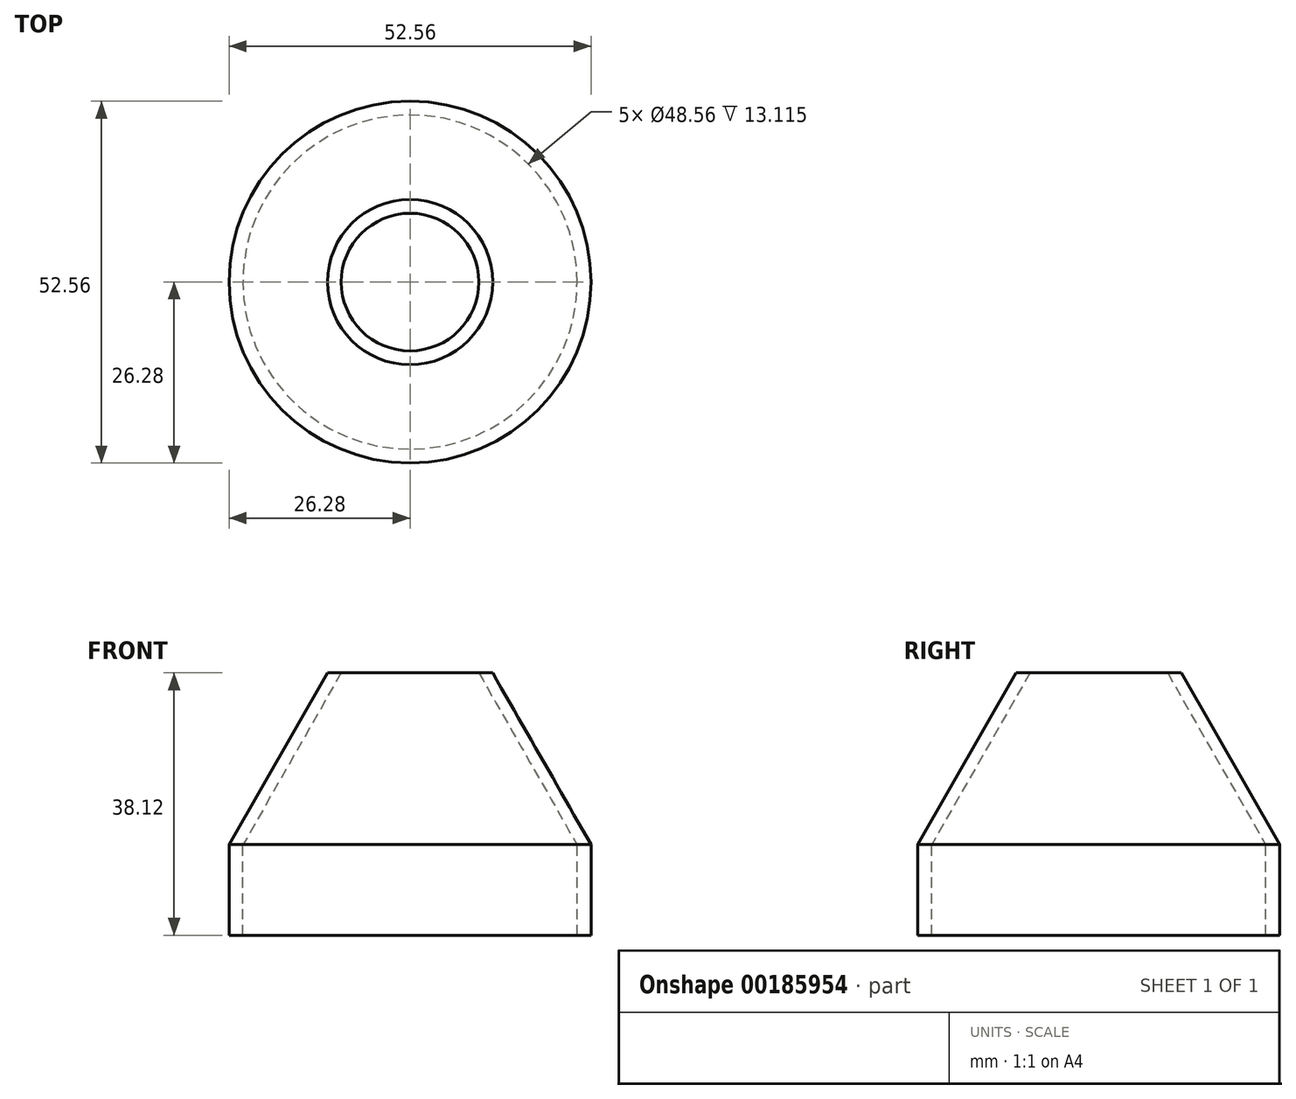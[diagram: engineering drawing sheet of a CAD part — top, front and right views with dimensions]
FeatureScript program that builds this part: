
annotation { "Feature Type Name" : "Feature", "Feature Type Description" : "" }
export const myFeature = defineFeature(function(context is Context, id is Id, definition is map)
    precondition{}
    {
        {
            var Q0;
            Q0=qCreatedBy(makeId("Front.planeOp"),FACE);
            var sketch = newSketch(context, id + "F0", { "sketchPlane" : qUnion([Q0])});
            skLineSegment(sketch, "E0", {"start": v(10, 63.59) * mm, "end": v(24.28, 38.59) * mm});
            skLineSegment(sketch, "E1.1", {"start": v(26.28, 38.65) * mm, "end": v(26.28, 25.47) * mm});
            skLineSegment(sketch, "E2", {"start": v(0, 48.1) * mm, "end": v(0, 23.18) * mm});
            skLineSegment(sketch, "E3", {"start": v(0, 48.1) * mm, "end": v(0, 66.71) * mm});
            skLineSegment(sketch, "E4", {"start": v(0, 66.71) * mm, "end": v(0, 71.68) * mm});
            skLineSegment(sketch, "E5", {"start": v(10, 63.59) * mm, "end": v(12, 63.59) * mm});
            skLineSegment(sketch, "E6", {"start": v(26.28, 0) * mm, "end": v(24.28, 0) * mm});
            skLineSegment(sketch, "E7", {"start": v(24.28, 25.47) * mm, "end": v(26.28, 25.47) * mm});
            skLineSegment(sketch, "E8", {"start": v(12, 63.59) * mm, "end": v(26.28, 38.65) * mm});
            skLineSegment(sketch, "E9", {"start": v(24.28, 38.59) * mm, "end": v(24.28, 25.47) * mm});
            skSolve(sketch);
        }
        {
            var Q0;
            {var subQ4=sQuery(id+"F0.wireOp",EDGE,"E0");Q0=makeQuery(id+"F0.imprint","IMPRINT",FACE,{"disambiguationData":[TD([[makeQuery(id+"F0.imprint","IMPRINT",EDGE,{"derivedFrom":subQ4}),1.0]])]});}
            var Q1;
            {var subQ3=sQuery(id+"F0.wireOp",EDGE,"hhz9abIA-96Le-VRXP-Uu4X-U4eWOdDqH8ju");Q1=makeQuery(id+"F0.imprint","IMPRINT",FACE,{"disambiguationData":[TD([[makeQuery(id+"F0.imprint","IMPRINT",EDGE,{"derivedFrom":subQ3}),1.0]])]});}
            var Q2;
            {var subQ1=sQuery(id+"F0.wireOp",EDGE,"E6");Q2=makeQuery(id+"F0.imprint","IMPRINT",FACE,{"disambiguationData":[TD([[makeQuery(id+"F0.imprint","IMPRINT",EDGE,{"derivedFrom":subQ1}),1.0]])]});}
            var Q3;
            Q3=sQuery(id+"F0.wireOp",EDGE,"E2");
            revolve(context, id + "F1", {"entities" : qUnion([Q0, Q1, Q2]), "axis" : qUnion([Q3]), "revolveType" : RevolveType.FULL});
        }
    });
